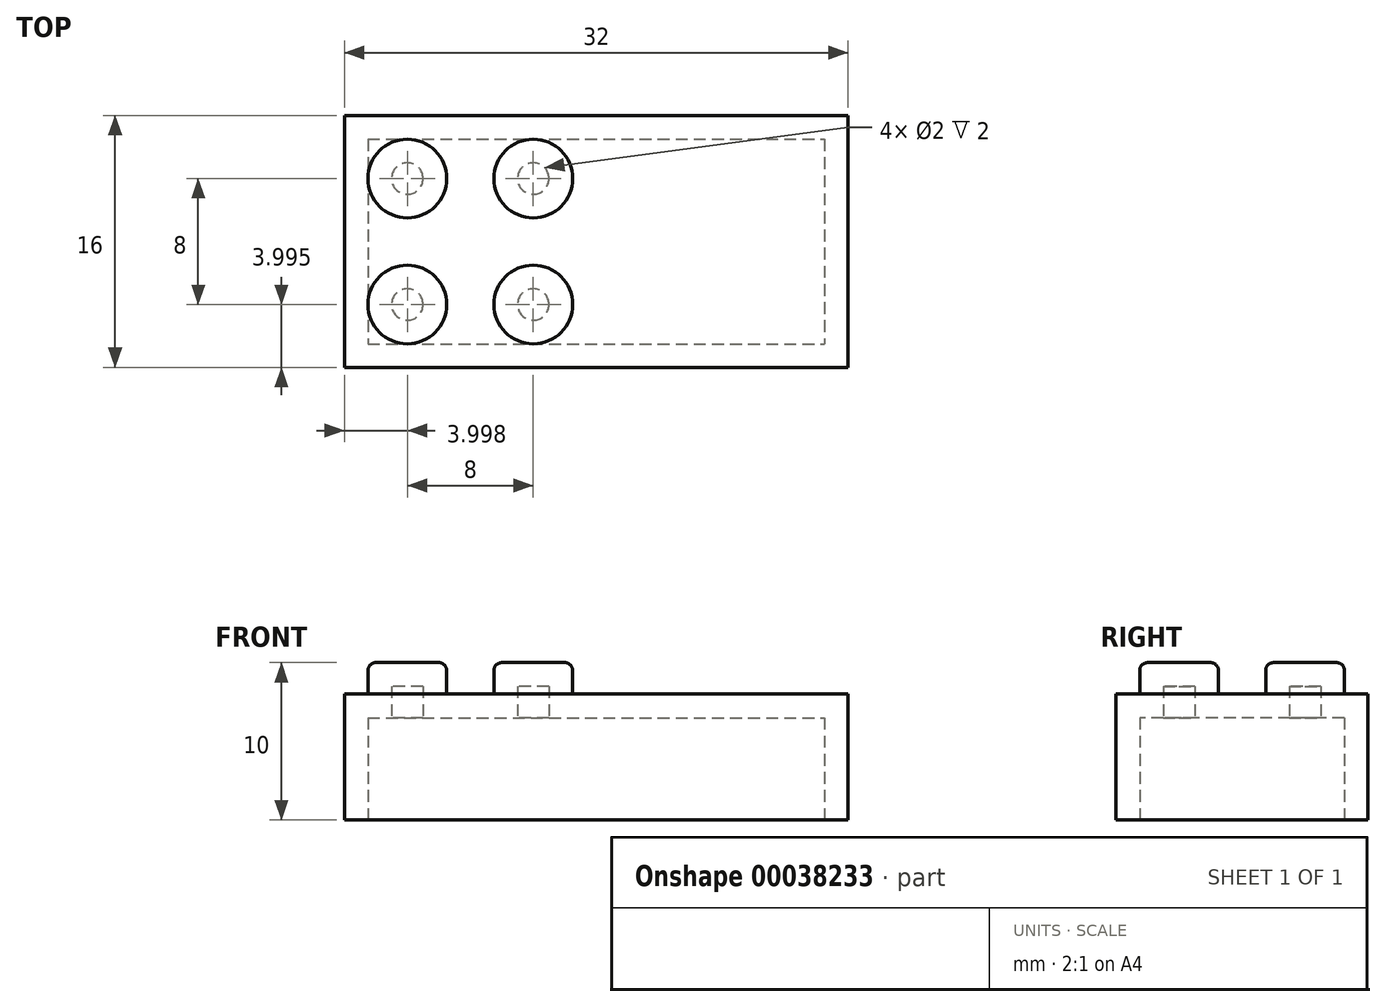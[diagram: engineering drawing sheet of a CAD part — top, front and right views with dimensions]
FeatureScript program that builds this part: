
annotation { "Feature Type Name" : "Feature", "Feature Type Description" : "" }
export const myFeature = defineFeature(function(context is Context, id is Id, definition is map)
    precondition{}
    {
        {
            var Q0;
            Q0=qCreatedBy(makeId("Top.planeOp"),FACE);
            cPlane(context, id + "F0", {"entities" : qUnion([Q0]), "cplaneType" : CPlaneType.OFFSET, "offset" : 8 * mm, "width" : 150 * mm, "height" : 150 * mm});
        }
        {
            var Q0;
            Q0=qCreatedBy(makeId("Top.planeOp"),FACE);
            var sketch = newSketch(context, id + "F1", { "sketchPlane" : qUnion([Q0])});
            skLineSegment(sketch, "E0.bottom", {"start": v(-14.61, 7) * mm, "end": v(17.39, 7) * mm});
            skLineSegment(sketch, "E0.top", {"start": v(-14.61, -9) * mm, "end": v(17.39, -9) * mm});
            skLineSegment(sketch, "E0.left", {"start": v(-14.61, 7) * mm, "end": v(-14.61, -9) * mm});
            skLineSegment(sketch, "E0.right", {"start": v(17.39, 7) * mm, "end": v(17.39, -9) * mm});
            skSolve(sketch);
        }
        {
            var Q0;
            Q0 = qSketchRegion(id + "F1", true);
            extrude(context, id + "F2", {"entities" : qUnion([Q0]), "depth" : 8 * mm});
        }
        {
            var Q0;
            Q0=qCreatedBy(id+"F0.planeOp",FACE);
            var sketch = newSketch(context, id + "F3", { "sketchPlane" : qUnion([Q0])});
            skLineSegment(sketch, "E1", {"start": v(-38.36, 3) * mm, "end": v(47.81, 3) * mm, "construction": true});
            skLineSegment(sketch, "E2", {"start": v(-38.86, -1) * mm, "end": v(49.82, -1) * mm, "construction": true});
            skLineSegment(sketch, "E3", {"start": v(-37.67, -5) * mm, "end": v(47.55, -5) * mm, "construction": true});
            skLineSegment(sketch, "E4", {"start": v(-10.61, 11.27) * mm, "end": v(-10.61, -13.09) * mm, "construction": true});
            skLineSegment(sketch, "E5", {"start": v(-2.61, 11.27) * mm, "end": v(-2.61, -13.65) * mm, "construction": true});
            skLineSegment(sketch, "E6", {"start": v(5.39, 11.2) * mm, "end": v(5.39, -13.44) * mm, "construction": true});
            skLineSegment(sketch, "E7", {"start": v(13.39, 11.55) * mm, "end": v(13.39, -13.86) * mm, "construction": true});
            skCircle(sketch, "E8", {"center": v(-10.61, 3) * mm, "radius": 2.5 * mm});
            skCircle(sketch, "E9", {"center": v(-10.61, -5) * mm, "radius": 2.5 * mm});
            skCircle(sketch, "E10", {"center": v(-2.61, 3) * mm, "radius": 2.5 * mm});
            skCircle(sketch, "E11", {"center": v(-2.61, -5) * mm, "radius": 2.5 * mm});
            skLineSegment(sketch, "E12", {"start": v(1.39, 11.2) * mm, "end": v(1.39, -13.58) * mm});
            skCircle(sketch, "E13.MirrorC", {"center": v(5.39, 3) * mm, "radius": 2.5 * mm});
            skCircle(sketch, "E14.MirrorC", {"center": v(5.39, -5) * mm, "radius": 2.5 * mm});
            skCircle(sketch, "E15.MirrorC", {"center": v(13.39, -5) * mm, "radius": 2.5 * mm});
            skCircle(sketch, "E16.MirrorC", {"center": v(13.39, 3) * mm, "radius": 2.5 * mm});
            skSolve(sketch);
        }
        {
            var Q0;
            Q0=makeQuery(id+"F3.imprint","IMPRINT",FACE,{"disambiguationData":[TD([[makeQuery(id+"F3.imprint","IMPRINT",EDGE,{"derivedFrom":sQuery(id+"F3.wireOp",EDGE,"E8")}),1.0]])]});
            var Q1;
            Q1=makeQuery(id+"F3.imprint","IMPRINT",FACE,{"disambiguationData":[TD([[makeQuery(id+"F3.imprint","IMPRINT",EDGE,{"derivedFrom":sQuery(id+"F3.wireOp",EDGE,"E10")}),1.0]])]});
            var Q2;
            Q2=makeQuery(id+"F3.imprint","IMPRINT",FACE,{"disambiguationData":[TD([[makeQuery(id+"F3.imprint","IMPRINT",EDGE,{"derivedFrom":sQuery(id+"F3.wireOp",EDGE,"E13.MirrorC")}),-1.0]])]});
            var Q3;
            Q3=makeQuery(id+"F3.imprint","IMPRINT",FACE,{"disambiguationData":[TD([[makeQuery(id+"F3.imprint","IMPRINT",EDGE,{"derivedFrom":sQuery(id+"F3.wireOp",EDGE,"E16.MirrorC")}),-1.0]])]});
            var Q4;
            Q4=makeQuery(id+"F3.imprint","IMPRINT",FACE,{"disambiguationData":[TD([[makeQuery(id+"F3.imprint","IMPRINT",EDGE,{"derivedFrom":sQuery(id+"F3.wireOp",EDGE,"E15.MirrorC")}),-1.0]])]});
            var Q5;
            Q5=makeQuery(id+"F3.imprint","IMPRINT",FACE,{"disambiguationData":[TD([[makeQuery(id+"F3.imprint","IMPRINT",EDGE,{"derivedFrom":sQuery(id+"F3.wireOp",EDGE,"E14.MirrorC")}),-1.0]])]});
            var Q6;
            Q6=makeQuery(id+"F3.imprint","IMPRINT",FACE,{"disambiguationData":[TD([[makeQuery(id+"F3.imprint","IMPRINT",EDGE,{"derivedFrom":sQuery(id+"F3.wireOp",EDGE,"E11")}),1.0]])]});
            var Q7;
            Q7=makeQuery(id+"F3.imprint","IMPRINT",FACE,{"disambiguationData":[TD([[makeQuery(id+"F3.imprint","IMPRINT",EDGE,{"derivedFrom":sQuery(id+"F3.wireOp",EDGE,"E9")}),1.0]])]});
            extrude(context, id + "F4", {"entities" : qUnion([Q0, Q1, Q2, Q3, Q4, Q5, Q6, Q7]), "operationType" : NewBodyOperationType.ADD, "depth" : 2 * mm});
        }
        {
            var Q0;
            Q0=makeQuery(id+"F4.opExtrude","CAP_EDGE",EDGE,{"disambiguationData":[OSD([sQuery(id+"F3.wireOp",EDGE,"E8")])],"isStart":false});
            var Q1;
            Q1=makeQuery(id+"F4.opExtrude","CAP_EDGE",EDGE,{"disambiguationData":[OSD([sQuery(id+"F3.wireOp",EDGE,"E9")])],"isStart":false});
            var Q2;
            Q2=makeQuery(id+"F4.opExtrude","CAP_EDGE",EDGE,{"disambiguationData":[OSD([sQuery(id+"F3.wireOp",EDGE,"E10")])],"isStart":false});
            var Q3;
            Q3=makeQuery(id+"F4.opExtrude","CAP_EDGE",EDGE,{"disambiguationData":[OSD([sQuery(id+"F3.wireOp",EDGE,"E11")])],"isStart":false});
            var Q4;
            Q4=makeQuery(id+"F4.opExtrude","CAP_FACE",FACE,{"disambiguationData":[OSD([sQuery(id+"F3.wireOp",EDGE,"E13.MirrorC")])],"isStart":false});
            var Q5;
            Q5=makeQuery(id+"F4.opExtrude","CAP_EDGE",EDGE,{"disambiguationData":[OSD([sQuery(id+"F3.wireOp",EDGE,"E13.MirrorC")])],"isStart":false});
            var Q6;
            Q6=makeQuery(id+"F4.opExtrude","CAP_EDGE",EDGE,{"disambiguationData":[OSD([sQuery(id+"F3.wireOp",EDGE,"E14.MirrorC")])],"isStart":false});
            var Q7;
            Q7=makeQuery(id+"F4.opExtrude","CAP_EDGE",EDGE,{"disambiguationData":[OSD([sQuery(id+"F3.wireOp",EDGE,"E16.MirrorC")])],"isStart":false});
            var Q8;
            Q8=makeQuery(id+"F4.opExtrude","CAP_EDGE",EDGE,{"disambiguationData":[OSD([sQuery(id+"F3.wireOp",EDGE,"E15.MirrorC")])],"isStart":false});
            fillet(context, id + "F5", {"entities" : qUnion([Q0, Q1, Q2, Q3, Q4, Q5, Q6, Q7, Q8]), "radius" : 0.5 * mm, "tangentPropagation" : true, "allowEdgeOverflow" : false});
        }
        {
            var Q0;
            Q0=makeQuery(id+"F2.opExtrude","CAP_FACE",FACE,{"disambiguationData":[OSD([sQuery(id+"F1.wireOp",EDGE,"E0.bottom"),sQuery(id+"F1.wireOp",EDGE,"E0.top"),sQuery(id+"F1.wireOp",EDGE,"E0.left"),sQuery(id+"F1.wireOp",EDGE,"E0.right")])],"isStart":true});
            shell(context, id + "F6", {"entities" : qUnion([Q0]), "thickness" : 1.5 * mm});
        }
    });
